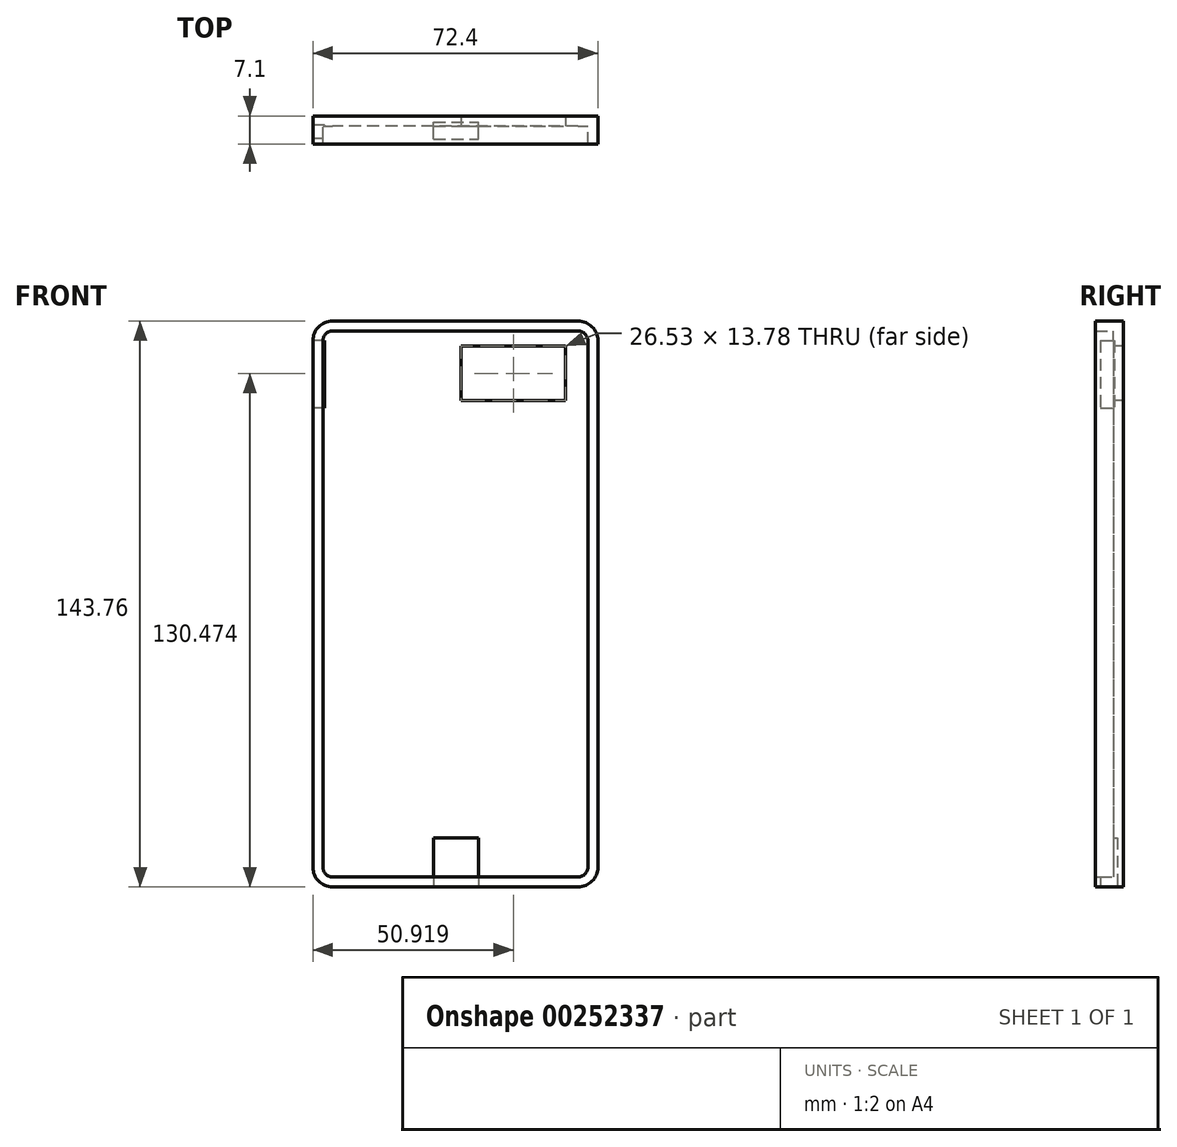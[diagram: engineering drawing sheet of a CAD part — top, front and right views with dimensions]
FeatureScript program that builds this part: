
annotation { "Feature Type Name" : "Feature", "Feature Type Description" : "" }
export const myFeature = defineFeature(function(context is Context, id is Id, definition is map)
    precondition{}
    {
        {
            var Q0;
            Q0=qCreatedBy(makeId("Front.planeOp"),FACE);
            var sketch = newSketch(context, id + "F0", { "sketchPlane" : qUnion([Q0])});
            skLineSegment(sketch, "E0.bottom", {"start": v(36.2, 71.88) * mm, "end": v(-36.2, 71.88) * mm});
            skLineSegment(sketch, "E0.top", {"start": v(36.2, -71.88) * mm, "end": v(-36.2, -71.88) * mm});
            skLineSegment(sketch, "E0.left", {"start": v(36.2, 71.88) * mm, "end": v(36.2, -71.88) * mm});
            skLineSegment(sketch, "E0.right", {"start": v(-36.2, 71.88) * mm, "end": v(-36.2, -71.88) * mm});
            skPoint(sketch, "E0.middle", {"position": v(0, 0) * mm});
            skLineSegment(sketch, "E1.bottom", {"start": v(4, 62.94) * mm, "end": v(25.44, 62.94) * mm});
            skLineSegment(sketch, "E1.top", {"start": v(4, 54.25) * mm, "end": v(25.44, 54.25) * mm});
            skLineSegment(sketch, "E1.left", {"start": v(4, 62.94) * mm, "end": v(4, 54.25) * mm});
            skLineSegment(sketch, "E1.right", {"start": v(25.44, 62.94) * mm, "end": v(25.44, 54.25) * mm});
            skSolve(sketch);
        }
        {
            var Q0;
            Q0=makeQuery(id+"F0.imprint","IMPRINT",FACE,{"disambiguationData":[TD([[makeQuery(id+"F0.imprint","IMPRINT",EDGE,{"derivedFrom":sQuery(id+"F0.wireOp",EDGE,"E0.bottom")}),1.0]])]});
            extrude(context, id + "F1", {"entities" : qUnion([Q0]), "endBound" : BoundingType.SYMMETRIC, "depth" : 7.1 * mm});
        }
        {
            var Q0;
            Q0=makeQuery(id+"F1.opExtrude","SWEPT_EDGE",EDGE,{"disambiguationData":[OSD([sQuery(id+"F0.wireOp",EDGE,"E0.bottom"),sQuery(id+"F0.wireOp",EDGE,"E0.right")])]});
            var Q1;
            Q1=makeQuery(id+"F1.opExtrude","SWEPT_EDGE",EDGE,{"disambiguationData":[OSD([sQuery(id+"F0.wireOp",EDGE,"E0.bottom"),sQuery(id+"F0.wireOp",EDGE,"E0.left")])]});
            var Q2;
            Q2=makeQuery(id+"F1.opExtrude","SWEPT_EDGE",EDGE,{"disambiguationData":[OSD([sQuery(id+"F0.wireOp",EDGE,"E0.top"),sQuery(id+"F0.wireOp",EDGE,"E0.left")])]});
            var Q3;
            Q3=makeQuery(id+"F1.opExtrude","SWEPT_EDGE",EDGE,{"disambiguationData":[OSD([sQuery(id+"F0.wireOp",EDGE,"E0.top"),sQuery(id+"F0.wireOp",EDGE,"E0.right")])]});
            fillet(context, id + "F2", {"entities" : qUnion([Q0, Q1, Q2, Q3]), "radius" : 5 * mm, "tangentPropagation" : true, "allowEdgeOverflow" : false});
        }
        {
            var Q0;
            Q0=makeQuery(id+"F1.opExtrude","CAP_FACE",FACE,{"disambiguationData":[OSD([sQuery(id+"F0.wireOp",EDGE,"E0.bottom"),sQuery(id+"F0.wireOp",EDGE,"E0.top"),sQuery(id+"F0.wireOp",EDGE,"E0.left"),sQuery(id+"F0.wireOp",EDGE,"E0.right")])],"isStart":false});
            shell(context, id + "F3", {"entities" : qUnion([Q0]), "thickness" : 2.54 * mm});
        }
        {
            var Q0;
            {var subQ0=sQuery(id+"F0.wireOp",EDGE,"E1.right");var subQ1=sQuery(id+"F0.wireOp",EDGE,"E1.left");var subQ2=sQuery(id+"F0.wireOp",EDGE,"E1.top");var subQ3=sQuery(id+"F0.wireOp",EDGE,"E1.bottom");var subQ4=sQuery(id+"F0.wireOp",EDGE,"E0.right");var subQ5=sQuery(id+"F0.wireOp",EDGE,"E0.left");var subQ6=sQuery(id+"F0.wireOp",EDGE,"E0.top");var subQ7=sQuery(id+"F0.wireOp",EDGE,"E0.bottom");Q0=makeQuery(id+"F3.opShell","OFFSET_FACE",FACE,{"disambiguationData":[OSD([subQ7,subQ6,subQ5,subQ4,subQ3,subQ2,subQ1,subQ0]),TDD([makeQuery(id+"F1.opExtrude","CAP_FACE",FACE,{"disambiguationData":[OSD([subQ7,subQ6,subQ5,subQ4,subQ3,subQ2,subQ1,subQ0])],"isStart":false})])]});}
            extrude(context, id + "F4", {"entities" : qUnion([Q0]), "operationType" : NewBodyOperationType.REMOVE, "oppositeDirection" : true, "depth" : 25 * mm});
        }
        {
            var Q0;
            Q0=makeQuery(id+"F1.opExtrude","SWEPT_FACE",FACE,{"disambiguationData":[OSD([sQuery(id+"F0.wireOp",EDGE,"E0.top")])]});
            var sketch = newSketch(context, id + "F5", { "sketchPlane" : qUnion([Q0])});
            skLineSegment(sketch, "E2.bottom", {"start": v(-5.55, 2.31) * mm, "end": v(5.91, 2.31) * mm});
            skLineSegment(sketch, "E2.top", {"start": v(-5.55, -2.01) * mm, "end": v(5.91, -2.01) * mm});
            skLineSegment(sketch, "E2.left", {"start": v(-5.55, 2.31) * mm, "end": v(-5.55, -2.01) * mm});
            skLineSegment(sketch, "E2.right", {"start": v(5.91, 2.31) * mm, "end": v(5.91, -2.01) * mm});
            skSolve(sketch);
        }
        {
            var Q0;
            Q0=makeQuery(id+"F5.imprint","IMPRINT",FACE,{"disambiguationData":[TD([[makeQuery(id+"F5.imprint","IMPRINT",EDGE,{"derivedFrom":sQuery(id+"F5.wireOp",EDGE,"E2.bottom")}),-1.0]])]});
            extrude(context, id + "F6", {"entities" : qUnion([Q0]), "operationType" : NewBodyOperationType.REMOVE, "endBound" : BoundingType.SYMMETRIC, "oppositeDirection" : true, "depth" : 25 * mm});
        }
        {
            var Q0;
            Q0=makeQuery(id+"F1.opExtrude","SWEPT_FACE",FACE,{"disambiguationData":[OSD([sQuery(id+"F0.wireOp",EDGE,"E0.right")])]});
            var sketch = newSketch(context, id + "F7", { "sketchPlane" : qUnion([Q0])});
            skLineSegment(sketch, "E3.bottom", {"start": v(-1.3, 49.78) * mm, "end": v(2.23, 49.78) * mm});
            skLineSegment(sketch, "E3.top", {"start": v(-1.3, 66.88) * mm, "end": v(2.23, 66.88) * mm});
            skLineSegment(sketch, "E3.left", {"start": v(-1.3, 49.78) * mm, "end": v(-1.3, 66.88) * mm});
            skLineSegment(sketch, "E3.right", {"start": v(2.23, 49.78) * mm, "end": v(2.23, 66.88) * mm});
            skSolve(sketch);
        }
        {
            var Q0;
            Q0=makeQuery(id+"F7.imprint","IMPRINT",FACE,{"disambiguationData":[TD([[makeQuery(id+"F7.imprint","IMPRINT",EDGE,{"derivedFrom":sQuery(id+"F7.wireOp",EDGE,"E3.bottom")}),1.0]])]});
            extrude(context, id + "F8", {"entities" : qUnion([Q0]), "operationType" : NewBodyOperationType.REMOVE, "endBound" : BoundingType.SYMMETRIC, "oppositeDirection" : true, "depth" : 6 * mm});
        }
    });
